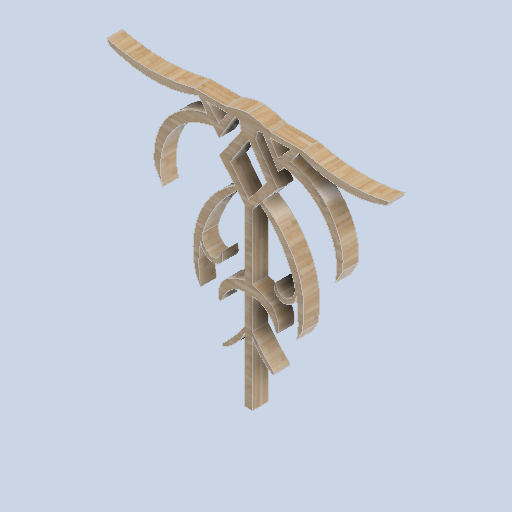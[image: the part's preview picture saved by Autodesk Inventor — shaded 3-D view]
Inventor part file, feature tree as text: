
AUTODESK INVENTOR PART (.ipt)
format: ipt  version: 2024.2 (Build 282272000, 272)  size: 598,016 bytes
history: native  units: mm
features: sketch x4, extrude x3, projected_geometry x2, plane x1
ambient origin geometry x8: Origin, YZ Plane, XZ Plane, XY Plane, X Axis, Y Axis, Z Axis, Center Point
bodies: Solid1 (feature_tree)
feature tree (10):
  extrude  "Extrusion1"  Depth=200.0mm TaperAngle=0.0deg
  extrude  "Extrusion2"  Depth=600.0mm
  extrude  "Extrusion3"  Depth=500.0mm
  plane  "Work Plane1"
  sketch  "Sketch4"  dims[d11=24.43461mm d12=0.0mm d13=0.0mm d14=200.0mm d15=0.0mm d16=-100.0mm]
  sketch  "Sketch1"  dims[d0=180.0deg d1=200.0mm d2=0.0mm]
  sketch  "Sketch2"  dims[d4=800.0mm d7=600.0mm]
  projected_geometry  "Projected Loop1"
  sketch  "Sketch3"  dims[d9=1400.0mm d10=500.0mm]
  projected_geometry  "Projected Loop2"
